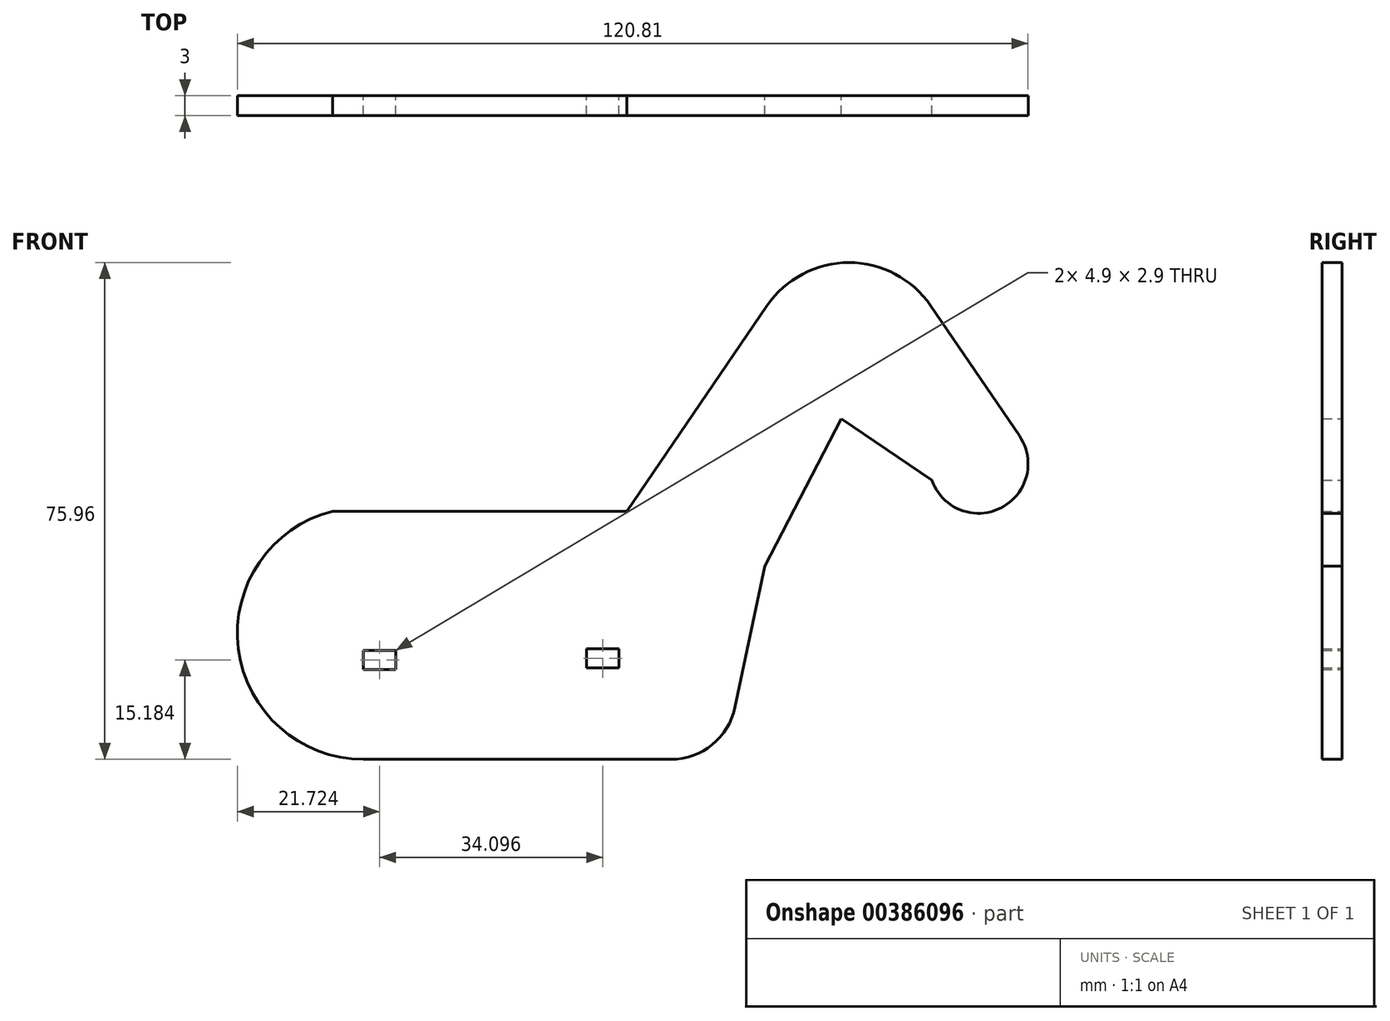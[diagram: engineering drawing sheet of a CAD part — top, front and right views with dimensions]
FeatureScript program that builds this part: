
annotation { "Feature Type Name" : "Feature", "Feature Type Description" : "" }
export const myFeature = defineFeature(function(context is Context, id is Id, definition is map)
    precondition{}
    {
        {
            var Q0;
            Q0=qCreatedBy(makeId("Front.planeOp"),FACE);
            var sketch = newSketch(context, id + "F0", { "sketchPlane" : qUnion([Q0])});
            skLineSegment(sketch, "E0", {"start": v(-39, -37.95) * mm, "end": v(16.1, -37.95) * mm});
            skArc(sketch, "E1", {"start": v(-39, -37.95) * mm, "mid": v(-58.12, -21.07) * mm, "end": v(-43.74, 0) * mm});
            skLineSegment(sketch, "E2", {"start": v(-43.74, 0) * mm, "end": v(1.26, 0) * mm});
            skLineSegment(sketch, "E3", {"start": v(1.26, 0) * mm, "end": v(22.66, 31.4) * mm});
            skArc(sketch, "E4", {"start": v(22.66, 31.4) * mm, "mid": v(35.16, 38) * mm, "end": v(47.66, 31.4) * mm});
            skLineSegment(sketch, "E5", {"start": v(47.66, 31.4) * mm, "end": v(61.23, 11.5) * mm});
            skArc(sketch, "E6", {"start": v(61.23, 11.5) * mm, "mid": v(58.39, 0.48) * mm, "end": v(47.83, 4.73) * mm});
            skLineSegment(sketch, "E7", {"start": v(47.83, 4.73) * mm, "end": v(40.71, 9.59) * mm});
            skLineSegment(sketch, "E8", {"start": v(40.71, 9.59) * mm, "end": v(34.02, 14.15) * mm});
            skLineSegment(sketch, "E9", {"start": v(34.02, 14.15) * mm, "end": v(22.3, -8.4) * mm});
            skLineSegment(sketch, "E10", {"start": v(22.3, -8.4) * mm, "end": v(16.1, -37.95) * mm});
            skSolve(sketch);
        }
        {
            var Q0;
            Q0 = qSketchRegion(id + "F0", true);
            extrude(context, id + "F1", {"entities" : qUnion([Q0]), "depth" : 3 * mm});
        }
        {
            var Q0;
            Q0=makeQuery(id+"F1.opExtrude","SWEPT_EDGE",EDGE,{"disambiguationData":[OSD([sQuery(id+"F0.wireOp",EDGE,"E0"),sQuery(id+"F0.wireOp",EDGE,"E10")])]});
            fillet(context, id + "F2", {"entities" : qUnion([Q0]), "radius" : 10 * mm, "tangentPropagation" : true, "allowEdgeOverflow" : false});
        }
        {
            var Q0;
            Q0=qCreatedBy(makeId("Front.planeOp"),FACE);
            var sketch = newSketch(context, id + "F3", { "sketchPlane" : qUnion([Q0])});
            skLineSegment(sketch, "E11.bottom", {"start": v(-34.1, -24.22) * mm, "end": v(-39, -24.22) * mm});
            skLineSegment(sketch, "E11.top", {"start": v(-34.1, -21.32) * mm, "end": v(-39, -21.32) * mm});
            skLineSegment(sketch, "E11.left", {"start": v(-34.1, -24.22) * mm, "end": v(-34.1, -21.32) * mm});
            skLineSegment(sketch, "E11.right", {"start": v(-39, -24.22) * mm, "end": v(-39, -21.32) * mm});
            skPoint(sketch, "E11.middle", {"position": v(-36.55, -22.77) * mm});
            skLineSegment(sketch, "E12.bottom", {"start": v(0, -21.08) * mm, "end": v(-4.9, -21.08) * mm});
            skLineSegment(sketch, "E12.top", {"start": v(0, -23.98) * mm, "end": v(-4.9, -23.98) * mm});
            skLineSegment(sketch, "E12.left", {"start": v(0, -21.08) * mm, "end": v(0, -23.98) * mm});
            skLineSegment(sketch, "E12.right", {"start": v(-4.9, -21.08) * mm, "end": v(-4.9, -23.98) * mm});
            skPoint(sketch, "E12.middle", {"position": v(-2.45, -22.53) * mm});
            skSolve(sketch);
        }
        {
            var Q0;
            Q0 = qSketchRegion(id + "F3", true);
            extrude(context, id + "F4", {"entities" : qUnion([Q0]), "operationType" : NewBodyOperationType.REMOVE, "oppositeDirection" : true, "depth" : 25 * mm});
        }
        {
            var Q0;
            Q0 = qSketchRegion(id + "F3", true);
            extrude(context, id + "F5", {"entities" : qUnion([Q0]), "operationType" : NewBodyOperationType.REMOVE, "depth" : 25 * mm});
        }
    });
